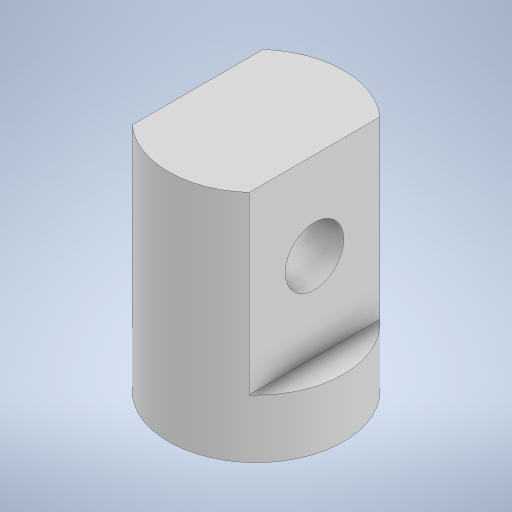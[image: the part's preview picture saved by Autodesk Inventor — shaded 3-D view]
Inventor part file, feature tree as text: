
AUTODESK INVENTOR PART (.ipt)
format: ipt  version: 2024 (Build 280153000, 153)  size: 245,248 bytes
history: native  units: mm
features: extrude x3, sketch x3, other x1
ambient origin geometry x8: Origin, YZ Plane, XZ Plane, XY Plane, X Axis, Y Axis, Z Axis, Center Point
bodies: Body1 (feature_tree)
feature tree (7):
  other  "솔리드1"
  extrude  "돌출1"  Depth=3.0mm
  extrude  "돌출5"  Depth=1.0mm TaperAngle=0.0deg
  extrude  "돌출6"  Depth=1.8mm
  sketch  "스케치2"
  sketch  "스케치4"
  sketch  "스케치6"
